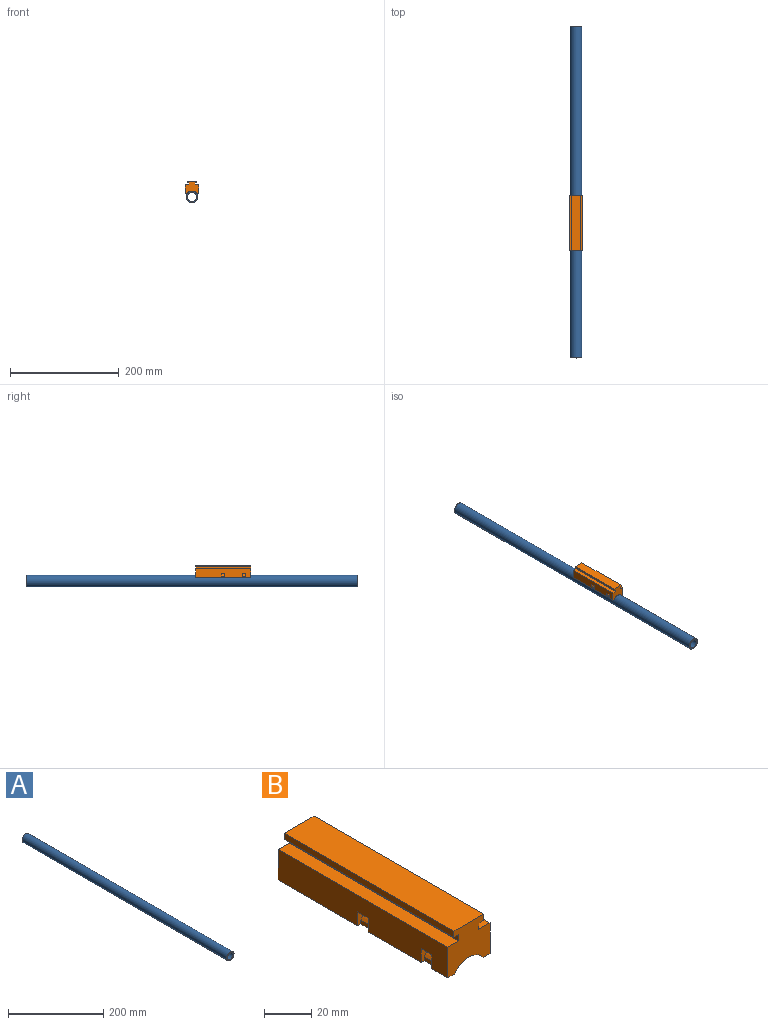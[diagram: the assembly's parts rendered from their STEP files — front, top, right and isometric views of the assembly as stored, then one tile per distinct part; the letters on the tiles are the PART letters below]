
ASSEMBLY  parts=2 mates=1
PART A: 4 faces, bbox 21.5x609.6x21.5 mm
  f0: cylinder r=8.21mm len=609.6mm, axis (0,1,0), area 31441.3mm2, adj f2,f3
  f1: cylinder r=10.73mm len=609.6mm, axis (0,1,0), area 41104.1mm2, adj f2,f3
  f2: plane 21.46x21.46mm, normal (0,-1,0), area 150.1mm2, adj f0,f1
  f3: plane 21.46x21.46mm, normal (0,1,0), area 150.1mm2, adj f0,f1
PART B: 28 faces, bbox 25.4x101.6x22.4 mm
  f0: plane 101.6x4.05mm, normal (0,0,-1), area 386.4mm2, adj f1,f4,f14,f15,f18,f20,f21,f24
  f1: plane 101.6x15.88mm, normal (1,0,0), area 1521.2mm2, adj f0,f5,f14,f15,f19,f20,f21,f25
  f2: plane 101.6x15.88mm, normal (-1,0,0), area 1521.2mm2, adj f3,f13,f14,f15,f19,f20,f21,f25
  f3: plane 101.6x4.05mm, normal (0,0,-1), area 386.4mm2, adj f2,f4,f14,f15,f16,f20,f21,f22
  f4: cylinder r=10.73mm len=101.6mm, axis (0,1,0), area 2044.6mm2, adj f0,f3,f14,f15
  f5: plane 101.6x6.6mm, normal (0,0,1), area 671mm2, adj f1,f6,f14,f15
  f6: plane 101.6x3.3mm, normal (1,0,0), area 335.5mm2, adj f5,f7,f14,f15
  f7: plane 101.6x2.79mm, normal (0,0,-1), area 283.9mm2, adj f6,f8,f14,f15
  f8: plane 101.6x3.18mm, normal (1,0,0), area 322.6mm2, adj f7,f9,f14,f15
  f9: plane 101.6x17.78mm, normal (0,0,1), area 1806.4mm2, adj f8,f10,f14,f15
  f10: plane 101.6x3.18mm, normal (-1,0,0), area 322.6mm2, adj f9,f11,f14,f15
  f11: plane 101.6x2.79mm, normal (0,0,-1), area 283.9mm2, adj f10,f12,f14,f15
  f12: plane 101.6x3.3mm, normal (-1,0,0), area 335.5mm2, adj f11,f13,f14,f15
  f13: plane 101.6x6.6mm, normal (0,0,1), area 671mm2, adj f2,f12,f14,f15
  f14: plane 25.4x22.35mm, normal (0,-1,0), area 446.9mm2, adj f0,f1,f2,f3,f4,f5,f6,f7
  f15: plane 25.4x22.35mm, normal (0,1,0), area 446.9mm2, adj f0,f1,f2,f3,f4,f5,f6,f7
  f16: plane 6.35x2.03mm, normal (-1,0,0), area 12.9mm2, adj f3,f17,f20,f21
  f17: cylinder r=12.7mm len=21.46mm, axis (0,1,0), area 162.3mm2, adj f16,f18,f20,f21
  f18: plane 6.35x2.03mm, normal (1,0,0), area 12.9mm2, adj f0,f17,f20,f21
  f19: cylinder r=17.46mm len=25.4mm, axis (0,1,0), area 180.6mm2, adj f1,f2,f20,f21
  f20: plane 25.4x12.7mm, normal (0,1,0), area 146.6mm2, adj f0,f1,f2,f3,f16,f17,f18,f19
  f21: plane 25.4x12.7mm, normal (0,-1,0), area 146.6mm2, adj f0,f1,f2,f3,f16,f17,f18,f19
  f22: plane 6.35x2.03mm, normal (-1,0,0), area 12.9mm2, adj f3,f23,f26,f27
  f23: cylinder r=12.7mm len=21.46mm, axis (0,-1,0), area 162.3mm2, adj f22,f24,f26,f27
  f24: plane 6.35x2.03mm, normal (1,0,0), area 12.9mm2, adj f0,f23,f26,f27
  f25: cylinder r=17.46mm len=25.4mm, axis (0,-1,0), area 180.6mm2, adj f1,f2,f26,f27
  f26: plane 25.4x12.7mm, normal (0,-1,0), area 146.6mm2, adj f0,f1,f2,f3,f22,f23,f24,f25
  f27: plane 25.4x12.7mm, normal (0,1,0), area 146.6mm2, adj f0,f1,f2,f3,f22,f23,f24,f25
PLACE A t=(-2,96.09,-10.29)mm
PLACE B t=(-2,38.71,-3.94)mm
MATE slider A.f1 <-> B.f4  axis (0,1,0) through (-2,96.09,-10.29)mm
